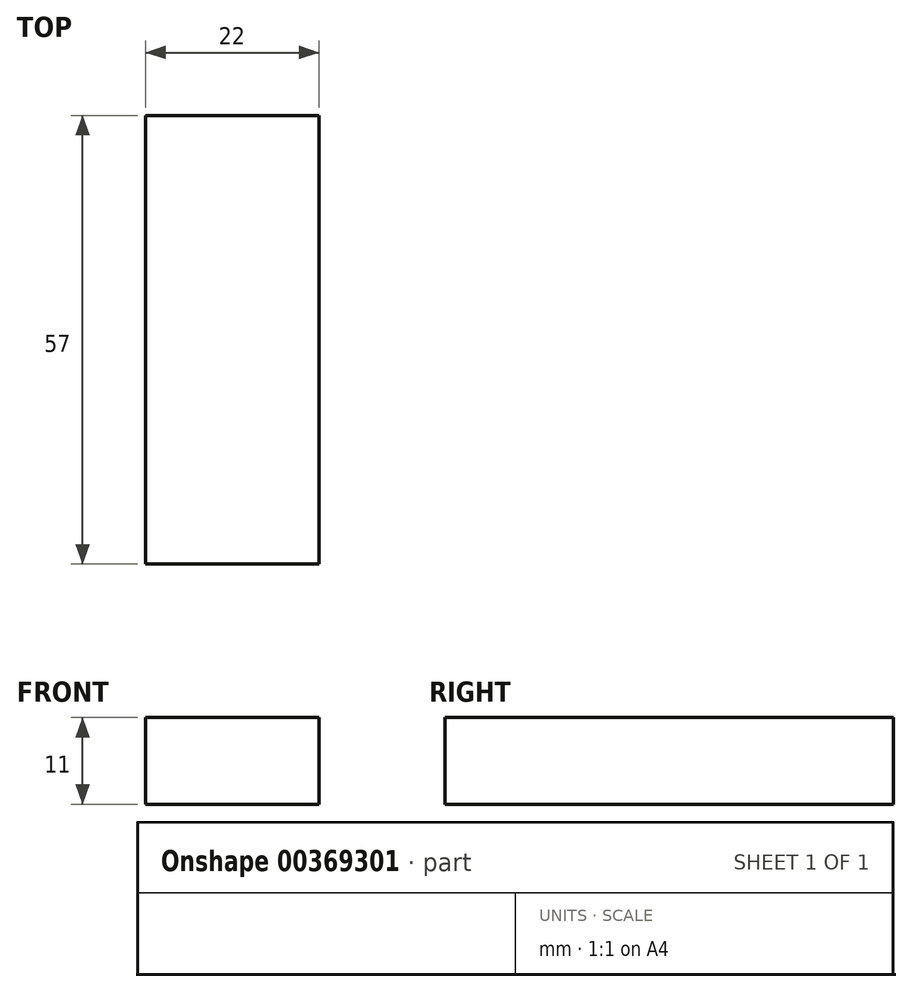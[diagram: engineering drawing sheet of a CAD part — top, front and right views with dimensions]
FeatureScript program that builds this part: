
annotation { "Feature Type Name" : "Feature", "Feature Type Description" : "" }
export const myFeature = defineFeature(function(context is Context, id is Id, definition is map)
    precondition{}
    {
        {
            var Q0;
            Q0=qCreatedBy(makeId("Right.planeOp"),FACE);
            var sketch = newSketch(context, id + "F0", { "sketchPlane" : qUnion([Q0])});
            skLineSegment(sketch, "E0.bottom", {"start": v(0, 11) * mm, "end": v(57, 11) * mm});
            skLineSegment(sketch, "E0.top", {"start": v(0, 0) * mm, "end": v(57, 0) * mm});
            skLineSegment(sketch, "E0.left", {"start": v(0, 11) * mm, "end": v(0, 0) * mm});
            skLineSegment(sketch, "E0.right", {"start": v(57, 11) * mm, "end": v(57, 0) * mm});
            skPoint(sketch, "E1", {"position": v(28.5, 11) * mm});
            skSolve(sketch);
        }
        {
            var Q0;
            Q0 = qSketchRegion(id + "F0", true);
            extrude(context, id + "F1", {"entities" : qUnion([Q0]), "depth" : 22 * mm});
        }
    });
